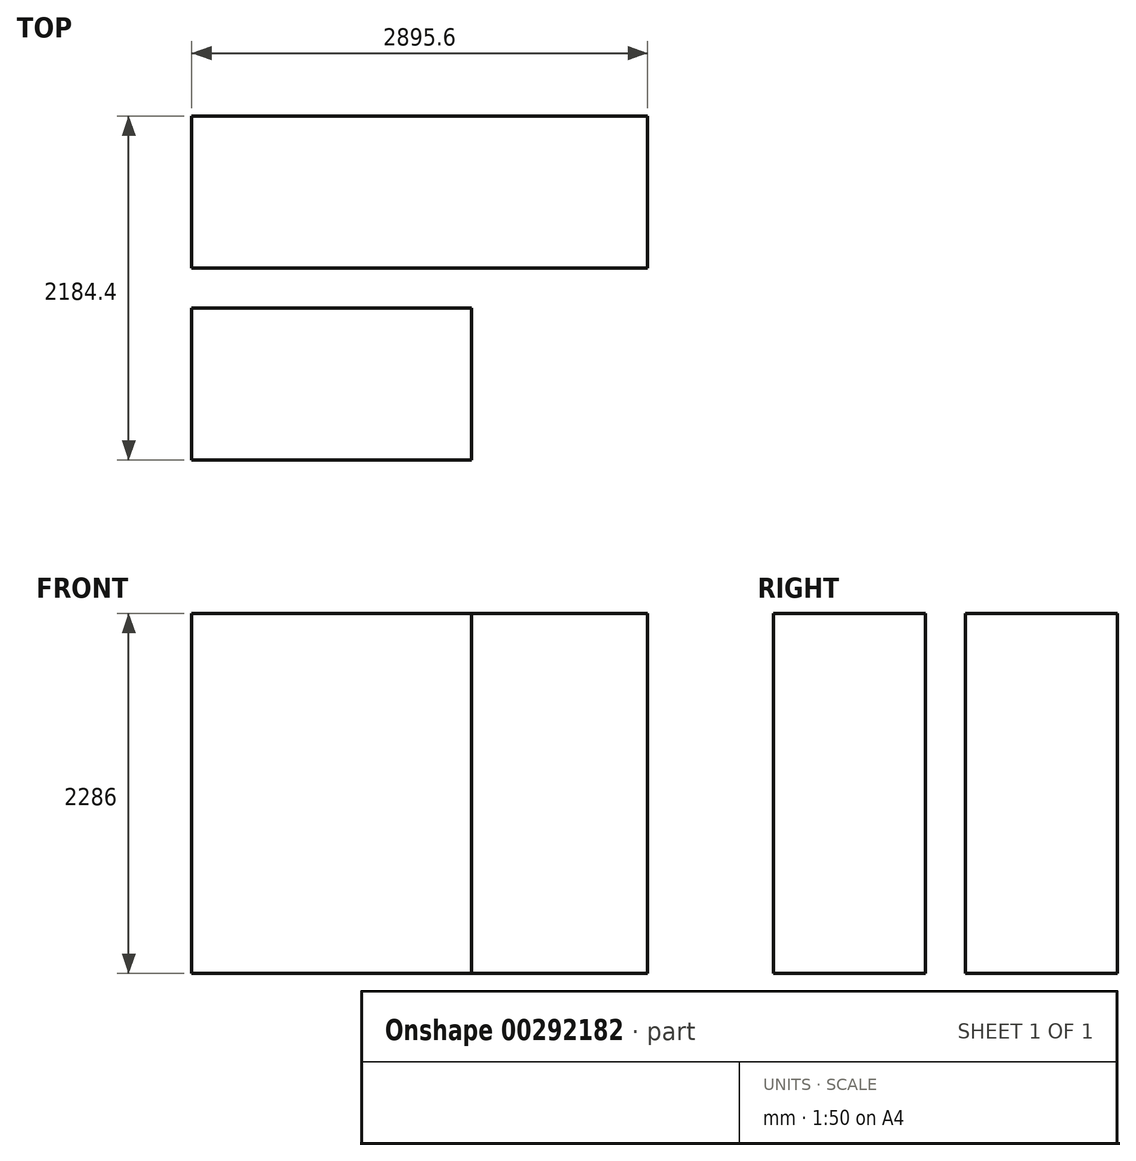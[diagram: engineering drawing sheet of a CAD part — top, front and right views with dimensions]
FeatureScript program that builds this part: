
annotation { "Feature Type Name" : "Feature", "Feature Type Description" : "" }
export const myFeature = defineFeature(function(context is Context, id is Id, definition is map)
    precondition{}
    {
        {
            var Q0;
            Q0=qCreatedBy(makeId("Top.planeOp"),FACE);
            var sketch = newSketch(context, id + "F0", { "sketchPlane" : qUnion([Q0])});
            skLineSegment(sketch, "E0.bottom", {"start": v(0, 0) * mm, "end": v(2895.6, 0) * mm});
            skLineSegment(sketch, "E0.top", {"start": v(0, 965.2) * mm, "end": v(2895.6, 965.2) * mm});
            skLineSegment(sketch, "E0.left", {"start": v(0, 0) * mm, "end": v(0, 965.2) * mm});
            skLineSegment(sketch, "E0.right", {"start": v(2895.6, 0) * mm, "end": v(2895.6, 965.2) * mm});
            skSolve(sketch);
        }
        {
            var Q0;
            Q0=makeQuery(id+"F0.imprint","IMPRINT",FACE,{"disambiguationData":[TD([[makeQuery(id+"F0.imprint","IMPRINT",EDGE,{"derivedFrom":sQuery(id+"F0.wireOp",EDGE,"E0.bottom")}),1.0]])]});
            extrude(context, id + "F1", {"entities" : qUnion([Q0]), "depth" : 2286 * mm});
        }
        {
            var Q0;
            Q0=qCreatedBy(makeId("Top.planeOp"),FACE);
            var sketch = newSketch(context, id + "F2", { "sketchPlane" : qUnion([Q0])});
            skLineSegment(sketch, "E1.bottom", {"start": v(0, 0) * mm, "end": v(254, 0) * mm, "construction": true});
            skLineSegment(sketch, "E1.top", {"start": v(0, -254) * mm, "end": v(254, -254) * mm, "construction": true});
            skLineSegment(sketch, "E1.left", {"start": v(0, 0) * mm, "end": v(0, -254) * mm, "construction": true});
            skLineSegment(sketch, "E1.right", {"start": v(254, 0) * mm, "end": v(254, -254) * mm, "construction": true});
            skLineSegment(sketch, "E2.bottom", {"start": v(0, -254) * mm, "end": v(1778, -254) * mm});
            skLineSegment(sketch, "E2.top", {"start": v(0, -1219.2) * mm, "end": v(1778, -1219.2) * mm});
            skLineSegment(sketch, "E2.left", {"start": v(0, -254) * mm, "end": v(0, -1219.2) * mm});
            skLineSegment(sketch, "E2.right", {"start": v(1778, -254) * mm, "end": v(1778, -1219.2) * mm});
            skSolve(sketch);
        }
        {
            var Q0;
            Q0=makeQuery(id+"F2.imprint","IMPRINT",FACE,{"disambiguationData":[TD([[makeQuery(id+"F2.imprint","IMPRINT",EDGE,{"derivedFrom":sQuery(id+"F2.wireOp",EDGE,"E2.bottom")}),-1.0]])]});
            extrude(context, id + "F3", {"entities" : qUnion([Q0]), "depth" : 2286 * mm});
        }
    });
